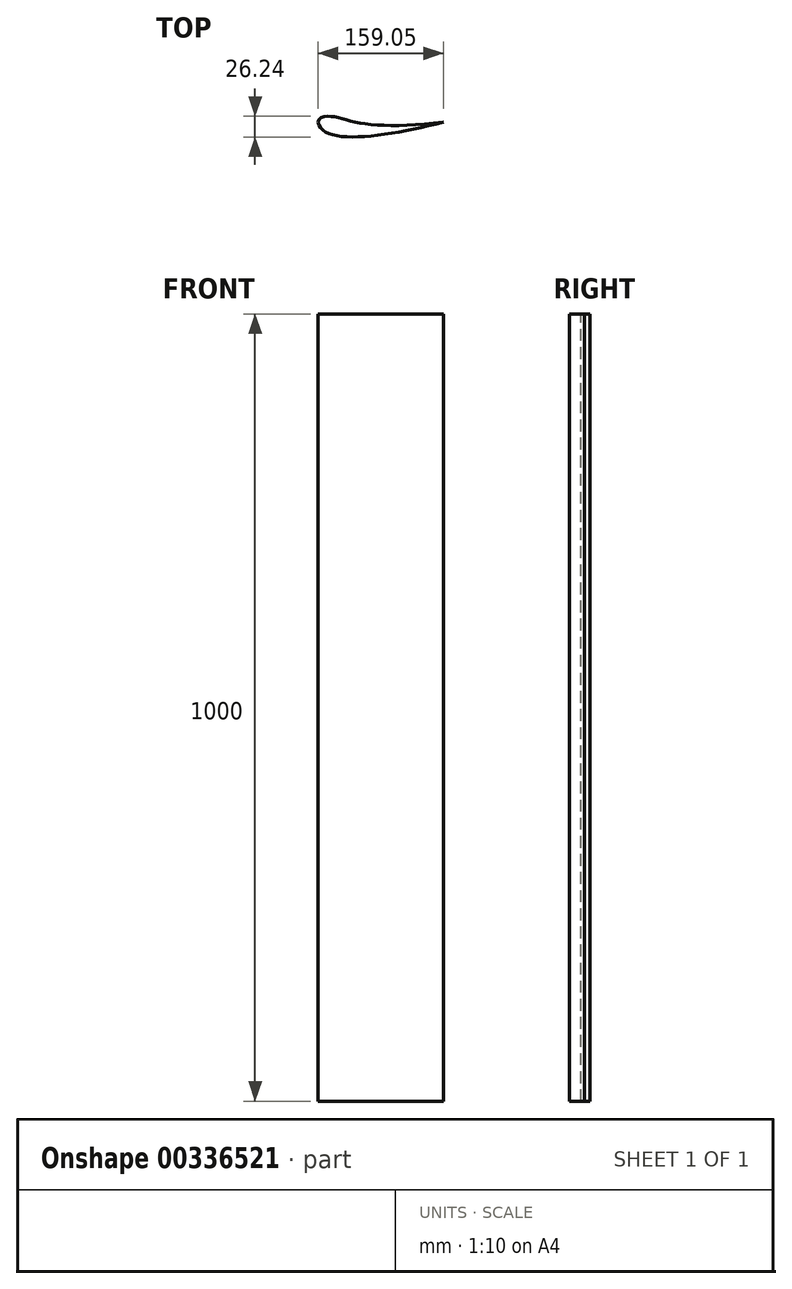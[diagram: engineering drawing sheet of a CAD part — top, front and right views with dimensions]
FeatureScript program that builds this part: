
annotation { "Feature Type Name" : "Feature", "Feature Type Description" : "" }
export const myFeature = defineFeature(function(context is Context, id is Id, definition is map)
    precondition{}
    {
        {
            var Q0;
            Q0=qCreatedBy(makeId("Top.planeOp"),FACE);
            var sketch = newSketch(context, id + "F0", { "sketchPlane" : qUnion([Q0])});
            skFitSpline(sketch, "E0", {"points": [v(0, 0) * mm, v(159.05, 0) * mm], "startDerivative": vector(15.93, -93.92) * mm, "endDerivative": vector(214.66, 55.34) * mm});
            skFitSpline(sketch, "E1", {"points": [v(0, 0) * mm, v(14.26, 7.27) * mm, v(46.68, 0) * mm, v(159.05, 0) * mm], "startDerivative": vector(0, 88.44) * mm, "endDerivative": vector(292.64, 36.35) * mm});
            skSolve(sketch);
        }
        {
            var Q0;
            Q0=makeQuery(id+"F0.imprint","IMPRINT",FACE,{"disambiguationData":[TD([[makeQuery(id+"F0.imprint","IMPRINT",EDGE,{"derivedFrom":sQuery(id+"F0.wireOp",EDGE,"E0")}),1.0]])]});
            extrude(context, id + "F1", {"entities" : qUnion([Q0]), "depth" : 1000 * mm});
        }
    });
